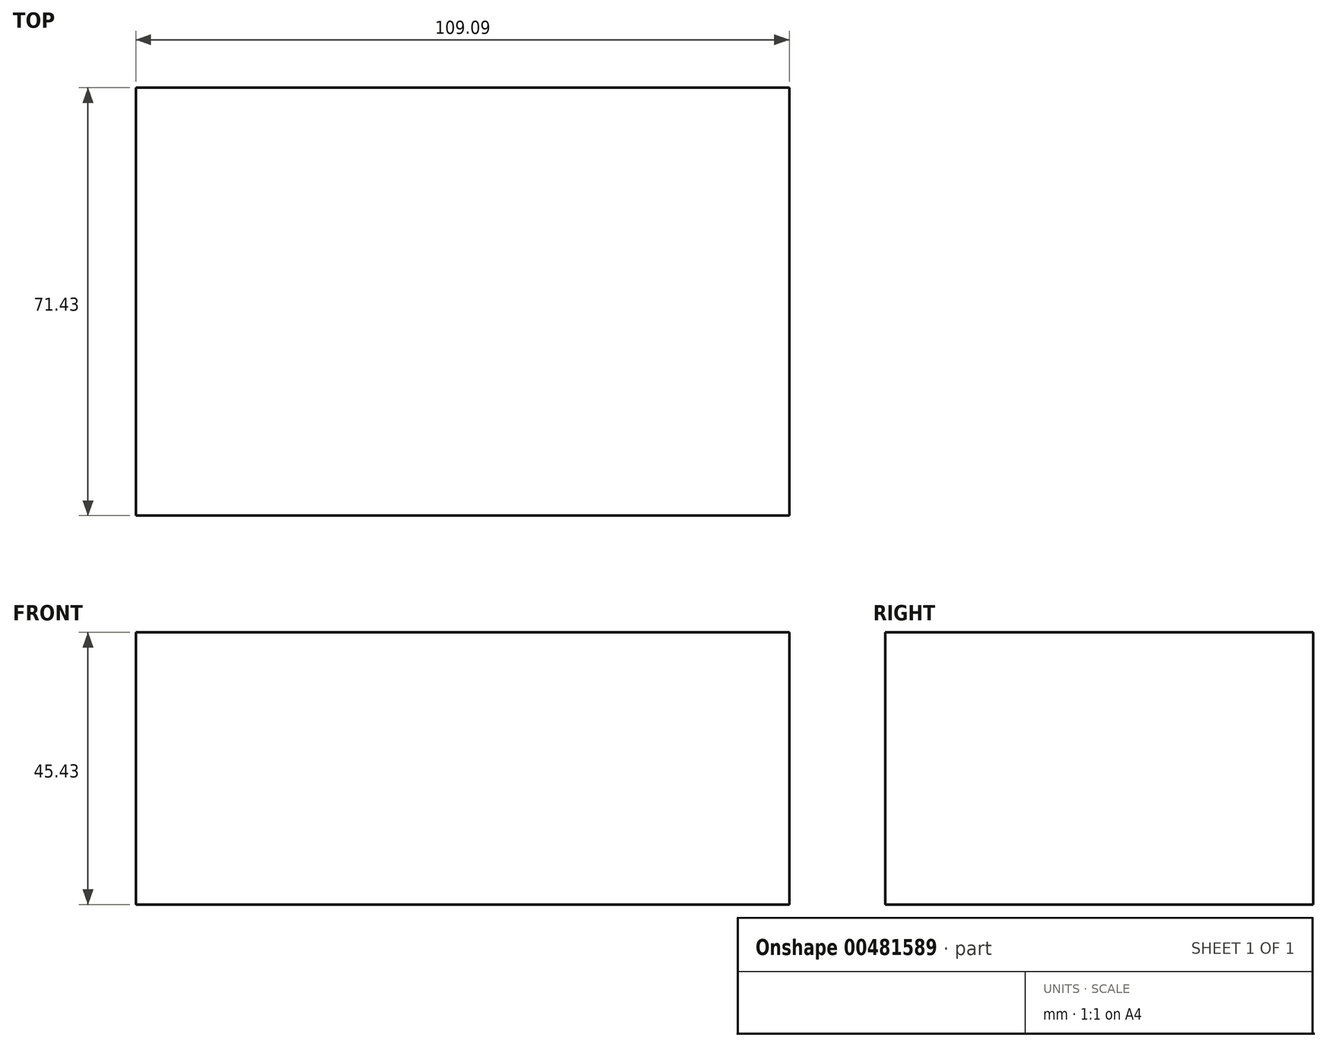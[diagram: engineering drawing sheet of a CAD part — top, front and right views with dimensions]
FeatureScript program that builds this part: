
annotation { "Feature Type Name" : "Feature", "Feature Type Description" : "" }
export const myFeature = defineFeature(function(context is Context, id is Id, definition is map)
    precondition{}
    {
        {
            var Q0;
            Q0=qCreatedBy(makeId("Top.planeOp"),FACE);
            var sketch = newSketch(context, id + "F0", { "sketchPlane" : qUnion([Q0])});
            skLineSegment(sketch, "E0.bottom", {"start": v(-49.4, 36.25) * mm, "end": v(59.7, 36.25) * mm});
            skLineSegment(sketch, "E0.top", {"start": v(-49.4, -35.18) * mm, "end": v(59.7, -35.18) * mm});
            skLineSegment(sketch, "E0.left", {"start": v(-49.4, 36.25) * mm, "end": v(-49.4, -35.18) * mm});
            skLineSegment(sketch, "E0.right", {"start": v(59.7, 36.25) * mm, "end": v(59.7, -35.18) * mm});
            skSolve(sketch);
        }
        {
            var Q0;
            Q0 = qSketchRegion(id + "F0", true);
            var sketch = newSketch(context, id + "F1", { "sketchPlane" : qUnion([Q0])});
            skSolve(sketch);
        }
        {
            var Q0;
            Q0=makeQuery(id+"F1.imprint","IMPRINT",FACE,{"disambiguationData":[TD([[makeQuery(id+"F1.imprint","IMPRINT",EDGE,{"derivedFrom":makeQuery(id+"F0.imprint","IMPRINT",EDGE,{"derivedFrom":sQuery(id+"F0.wireOp",EDGE,"E0.bottom")})}),-1.0]])]});
            extrude(context, id + "F2", {"entities" : qUnion([Q0]), "depth" : 45.43 * mm, "offsetDistance" : 25.4 * mm});
        }
    });
